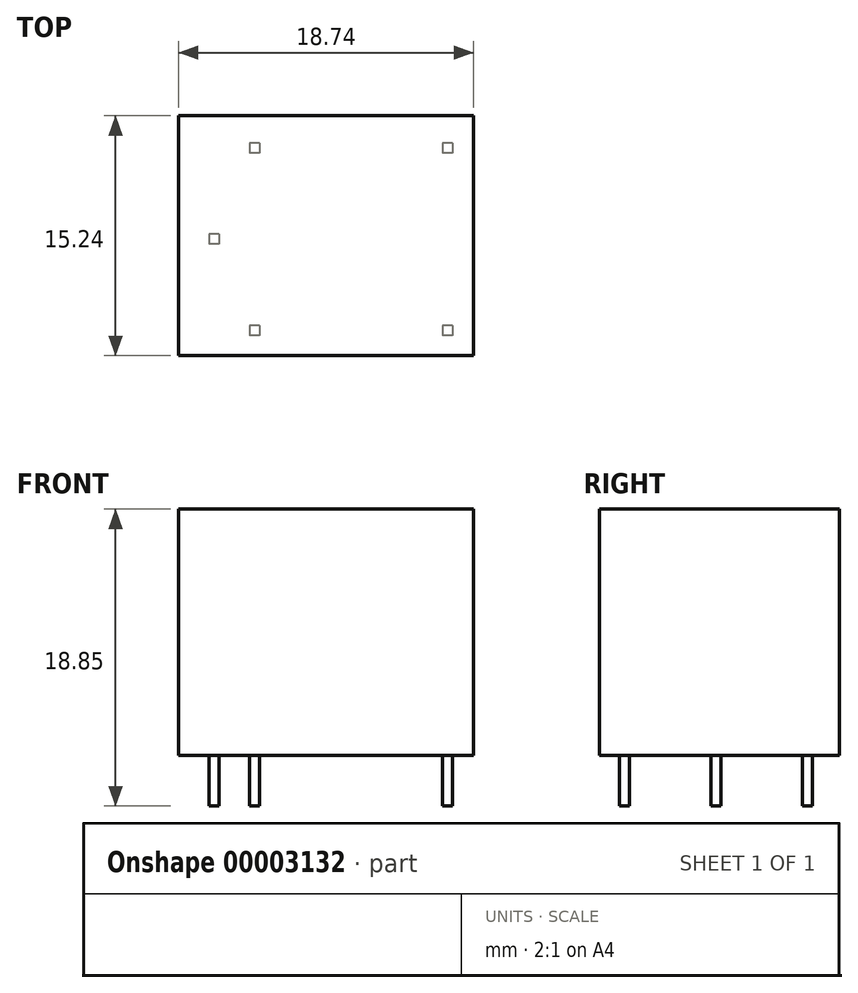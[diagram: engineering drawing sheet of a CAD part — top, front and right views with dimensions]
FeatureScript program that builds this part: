
annotation { "Feature Type Name" : "Feature", "Feature Type Description" : "" }
export const myFeature = defineFeature(function(context is Context, id is Id, definition is map)
    precondition{}
    {
        {
            var Q0;
            Q0=qCreatedBy(makeId("Top.planeOp"),FACE);
            var sketch = newSketch(context, id + "F0", { "sketchPlane" : qUnion([Q0])});
            skLineSegment(sketch, "E0.rect.bottom", {"start": v(9.37, -7.62) * mm, "end": v(-9.37, -7.62) * mm});
            skLineSegment(sketch, "E0.rect.top", {"start": v(9.37, 7.62) * mm, "end": v(-9.37, 7.62) * mm});
            skLineSegment(sketch, "E0.rect.left", {"start": v(9.37, -7.62) * mm, "end": v(9.37, 7.62) * mm});
            skLineSegment(sketch, "E0.rect.right", {"start": v(-9.37, -7.62) * mm, "end": v(-9.37, 7.62) * mm});
            skPoint(sketch, "E0.rect.middle", {"position": v(0, 0) * mm});
            skSolve(sketch);
        }
        {
            var Q0;
            Q0=makeQuery(id+"F0.imprint","IMPRINT",FACE,{"disambiguationData":[TD([[makeQuery(id+"F0.imprint","IMPRINT",EDGE,{"derivedFrom":sQuery(id+"F0.wireOp",EDGE,"E0.rect.bottom")}),-1.0]])]});
            extrude(context, id + "F1", {"entities" : qUnion([Q0]), "depth" : 15.65 * mm});
        }
        {
            var Q0;
            Q0=makeQuery(id+"F1.opExtrude","CAP_FACE",FACE,{"disambiguationData":[OSD([sQuery(id+"F0.wireOp",EDGE,"E0.rect.bottom"),sQuery(id+"F0.wireOp",EDGE,"E0.rect.top"),sQuery(id+"F0.wireOp",EDGE,"E0.rect.left"),sQuery(id+"F0.wireOp",EDGE,"E0.rect.right")])],"isStart":true});
            var sketch = newSketch(context, id + "F2", { "sketchPlane" : qUnion([Q0])});
            skLineSegment(sketch, "E1", {"start": v(19.33, 17.2) * mm, "end": v(19.33, -17.2) * mm, "construction": true});
            skLineSegment(sketch, "E2", {"start": v(19.33, -17.2) * mm, "end": v(-11.34, -17.2) * mm, "construction": true});
            skSolve(sketch);
        }
        {
            var Q0;
            Q0=makeQuery(id+"F1.opExtrude","CAP_FACE",FACE,{"disambiguationData":[OSD([sQuery(id+"F0.wireOp",EDGE,"E0.rect.bottom"),sQuery(id+"F0.wireOp",EDGE,"E0.rect.top"),sQuery(id+"F0.wireOp",EDGE,"E0.rect.left"),sQuery(id+"F0.wireOp",EDGE,"E0.rect.right")])],"isStart":true});
            var sketch = newSketch(context, id + "F3", { "sketchPlane" : qUnion([Q0])});
            skLineSegment(sketch, "E3.rect.bottom", {"start": v(8.03, 5.72) * mm, "end": v(7.4, 5.72) * mm});
            skLineSegment(sketch, "E3.rect.top", {"start": v(8.03, 6.35) * mm, "end": v(7.4, 6.35) * mm});
            skLineSegment(sketch, "E3.rect.left", {"start": v(8.03, 5.72) * mm, "end": v(8.03, 6.35) * mm});
            skLineSegment(sketch, "E3.rect.right", {"start": v(7.4, 5.72) * mm, "end": v(7.4, 6.35) * mm});
            skPoint(sketch, "E3.rect.middle", {"position": v(7.7, 6.03) * mm});
            skLineSegment(sketch, "E4.rect.bottom", {"start": v(8.03, -5.9) * mm, "end": v(7.4, -5.9) * mm});
            skLineSegment(sketch, "E4.rect.top", {"start": v(8.03, -5.26) * mm, "end": v(7.4, -5.26) * mm});
            skLineSegment(sketch, "E4.rect.left", {"start": v(8.03, -5.9) * mm, "end": v(8.03, -5.26) * mm});
            skLineSegment(sketch, "E4.rect.right", {"start": v(7.4, -5.9) * mm, "end": v(7.4, -5.26) * mm});
            skPoint(sketch, "E4.rect.middle", {"position": v(7.7, -5.58) * mm});
            skLineSegment(sketch, "E5.rect.bottom", {"start": v(-6.8, -0.09) * mm, "end": v(-7.44, -0.09) * mm});
            skLineSegment(sketch, "E5.rect.top", {"start": v(-6.8, 0.55) * mm, "end": v(-7.44, 0.55) * mm});
            skLineSegment(sketch, "E5.rect.left", {"start": v(-6.8, -0.09) * mm, "end": v(-6.8, 0.55) * mm});
            skLineSegment(sketch, "E5.rect.right", {"start": v(-7.44, -0.09) * mm, "end": v(-7.44, 0.55) * mm});
            skPoint(sketch, "E5.rect.middle", {"position": v(-7.12, 0.23) * mm});
            skLineSegment(sketch, "E6.rect.bottom", {"start": v(-4.22, 5.72) * mm, "end": v(-4.85, 5.72) * mm});
            skLineSegment(sketch, "E6.rect.top", {"start": v(-4.22, 6.35) * mm, "end": v(-4.85, 6.35) * mm});
            skLineSegment(sketch, "E6.rect.left", {"start": v(-4.22, 5.72) * mm, "end": v(-4.22, 6.35) * mm});
            skLineSegment(sketch, "E6.rect.right", {"start": v(-4.85, 5.72) * mm, "end": v(-4.85, 6.35) * mm});
            skPoint(sketch, "E6.rect.middle", {"position": v(-4.53, 6.03) * mm});
            skLineSegment(sketch, "E7.rect.bottom", {"start": v(-4.22, -5.9) * mm, "end": v(-4.85, -5.9) * mm});
            skLineSegment(sketch, "E7.rect.top", {"start": v(-4.22, -5.26) * mm, "end": v(-4.85, -5.26) * mm});
            skLineSegment(sketch, "E7.rect.left", {"start": v(-4.22, -5.9) * mm, "end": v(-4.22, -5.26) * mm});
            skLineSegment(sketch, "E7.rect.right", {"start": v(-4.85, -5.9) * mm, "end": v(-4.85, -5.26) * mm});
            skPoint(sketch, "E7.rect.middle", {"position": v(-4.53, -5.58) * mm});
            skSolve(sketch);
        }
        {
            var Q0;
            {Q0=qUnion([makeQuery(id+"F3.imprint","IMPRINT",FACE,{"disambiguationData":[TD([[makeQuery(id+"F3.imprint","IMPRINT",EDGE,{"derivedFrom":sQuery(id+"F3.wireOp",EDGE,"E3.rect.bottom")}),-1.0]])]}),makeQuery(id+"F3.imprint","IMPRINT",FACE,{"disambiguationData":[TD([[makeQuery(id+"F3.imprint","IMPRINT",EDGE,{"derivedFrom":sQuery(id+"F3.wireOp",EDGE,"E4.rect.bottom")}),-1.0]])]}),makeQuery(id+"F3.imprint","IMPRINT",FACE,{"disambiguationData":[TD([[makeQuery(id+"F3.imprint","IMPRINT",EDGE,{"derivedFrom":sQuery(id+"F3.wireOp",EDGE,"E5.rect.bottom")}),-1.0]])]}),makeQuery(id+"F3.imprint","IMPRINT",FACE,{"disambiguationData":[TD([[makeQuery(id+"F3.imprint","IMPRINT",EDGE,{"derivedFrom":sQuery(id+"F3.wireOp",EDGE,"E6.rect.bottom")}),-1.0]])]}),makeQuery(id+"F3.imprint","IMPRINT",FACE,{"disambiguationData":[TD([[makeQuery(id+"F3.imprint","IMPRINT",EDGE,{"derivedFrom":sQuery(id+"F3.wireOp",EDGE,"E7.rect.bottom")}),-1.0]])]})]);}
            extrude(context, id + "F4", {"entities" : qUnion([Q0]), "operationType" : NewBodyOperationType.ADD, "depth" : 3.2 * mm});
        }
    });
